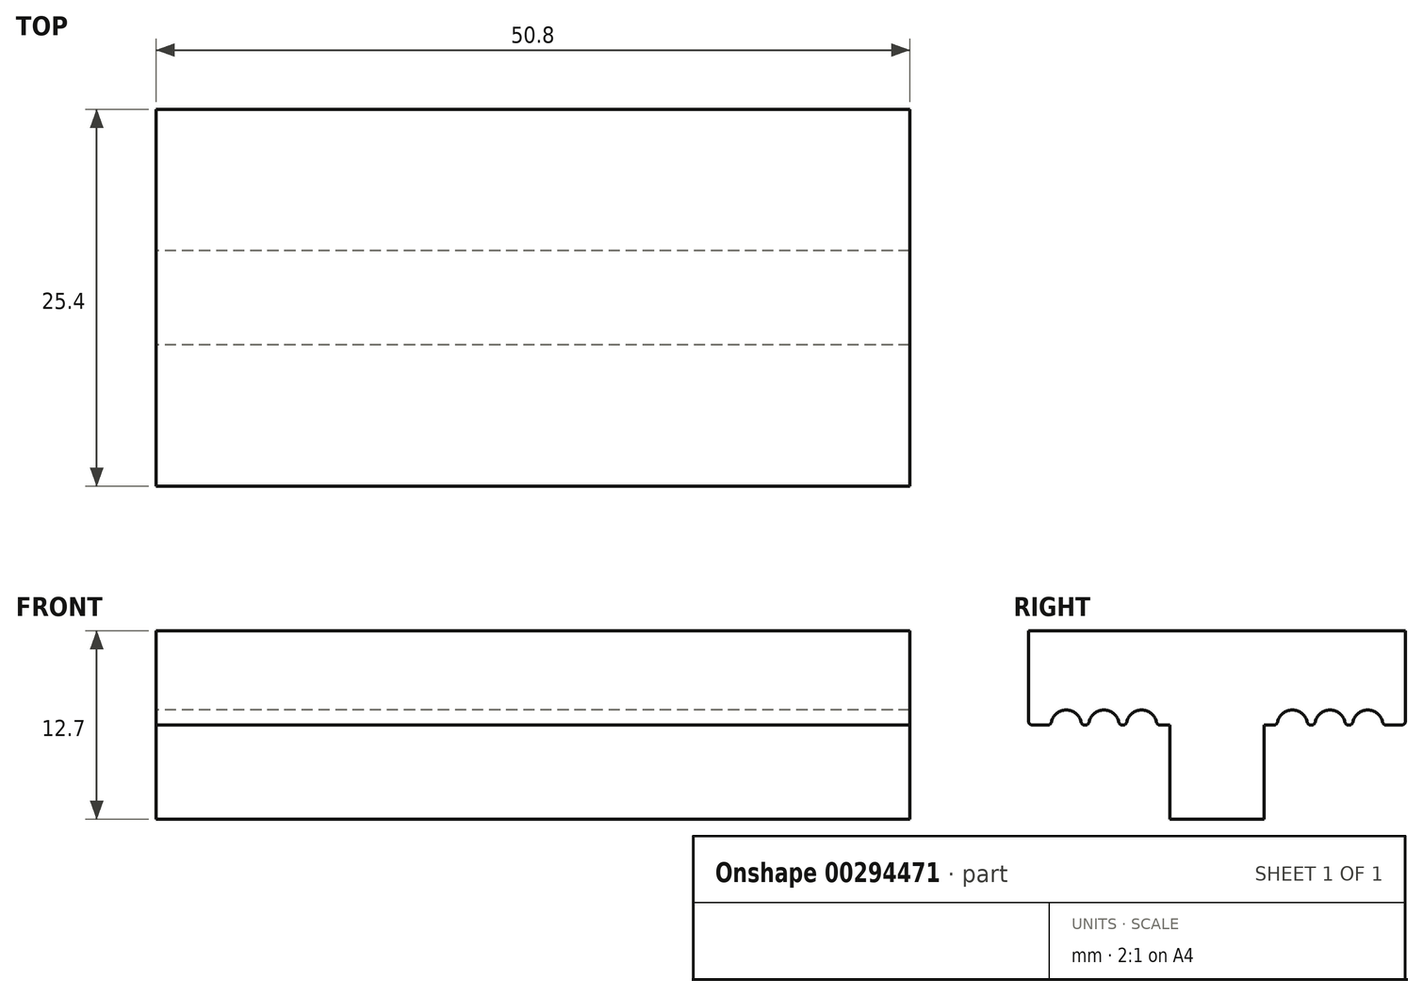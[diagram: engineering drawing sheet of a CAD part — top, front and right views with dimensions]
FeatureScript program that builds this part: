
annotation { "Feature Type Name" : "Feature", "Feature Type Description" : "" }
export const myFeature = defineFeature(function(context is Context, id is Id, definition is map)
    precondition{}
    {
        {
            var Q0;
            Q0=qCreatedBy(makeId("Right.planeOp"),FACE);
            var sketch = newSketch(context, id + "F0", { "sketchPlane" : qUnion([Q0])});
            skLineSegment(sketch, "E0.bottom", {"start": v(0, 0) * mm, "end": v(9.53, 0) * mm});
            skLineSegment(sketch, "E0.top", {"start": v(0, 6.35) * mm, "end": v(25.4, 6.35) * mm});
            skLineSegment(sketch, "E0.left", {"start": v(0, 0) * mm, "end": v(0, 6.35) * mm});
            skLineSegment(sketch, "E0.right", {"start": v(25.4, 0) * mm, "end": v(25.4, 6.35) * mm});
            skLineSegment(sketch, "E1.top", {"start": v(9.53, -6.35) * mm, "end": v(15.88, -6.35) * mm});
            skLineSegment(sketch, "E1.left", {"start": v(9.53, 0) * mm, "end": v(9.53, -6.35) * mm});
            skLineSegment(sketch, "E1.right", {"start": v(15.88, 0) * mm, "end": v(15.88, -6.35) * mm});
            skLineSegment(sketch, "E2", {"start": v(12.7, 6.35) * mm, "end": v(12.7, -6.35) * mm, "construction": true});
            skLineSegment(sketch, "E3.trimOffspring", {"start": v(15.88, 0) * mm, "end": v(25.4, 0) * mm});
            skArc(sketch, "E4", {"start": v(23.88, 0) * mm, "mid": v(22.86, 1.02) * mm, "end": v(21.84, 0) * mm});
            skArc(sketch, "E5", {"start": v(21.34, 0) * mm, "mid": v(20.32, 1.02) * mm, "end": v(19.3, 0) * mm});
            skArc(sketch, "E6", {"start": v(18.8, 0) * mm, "mid": v(17.78, 1.02) * mm, "end": v(16.76, 0) * mm});
            skArc(sketch, "E7.MirrorCS", {"start": v(1.52, 0) * mm, "mid": v(2.54, 1.02) * mm, "end": v(3.56, 0) * mm});
            skArc(sketch, "E8.MirrorCS", {"start": v(6.6, 0) * mm, "mid": v(7.62, 1.02) * mm, "end": v(8.64, 0) * mm});
            skArc(sketch, "E9.MirrorCS", {"start": v(4.06, 0) * mm, "mid": v(5.08, 1.02) * mm, "end": v(6.1, 0) * mm});
            skSolve(sketch);
        }
        {
            var Q0;
            Q0=makeQuery(id+"F0.imprint","IMPRINT",FACE,{"disambiguationData":[TD([[makeQuery(id+"F0.imprint","IMPRINT",EDGE,{"derivedFrom":sQuery(id+"F0.wireOp",EDGE,"E0.top")}),-1.0]])]});
            extrude(context, id + "F1", {"entities" : qUnion([Q0]), "depth" : 50.8 * mm});
        }
        {
            var Q0;
            {var subQ0=sQuery(id+"F0.wireOp",EDGE,"E4");var subQ1=sQuery(id+"F0.wireOp",EDGE,"E3.trimOffspring");Q0=makeQuery(id+"F1.opExtrude","SWEPT_EDGE",EDGE,{"disambiguationData":[OSD([subQ1,subQ0]),TDD([makeQuery(id+"F0.imprint","INTERSECT",VERTEX,{"disambiguationData":[OD(0.0)],"derivedFrom":[subQ1,subQ0]})])]});}
            var Q1;
            Q1=makeQuery(id+"F1.opExtrude","SWEPT_EDGE",EDGE,{"disambiguationData":[OSD([sQuery(id+"F0.wireOp",EDGE,"E0.right"),sQuery(id+"F0.wireOp",EDGE,"E3.trimOffspring")])]});
            var Q2;
            {var subQ0=sQuery(id+"F0.wireOp",EDGE,"E4");var subQ1=sQuery(id+"F0.wireOp",EDGE,"E3.trimOffspring");Q2=makeQuery(id+"F1.opExtrude","SWEPT_EDGE",EDGE,{"disambiguationData":[OSD([subQ1,subQ0]),TDD([makeQuery(id+"F0.imprint","INTERSECT",VERTEX,{"disambiguationData":[OD(1.0)],"derivedFrom":[subQ1,subQ0]})])]});}
            var Q3;
            {var subQ0=sQuery(id+"F0.wireOp",EDGE,"E5");var subQ1=sQuery(id+"F0.wireOp",EDGE,"E3.trimOffspring");Q3=makeQuery(id+"F1.opExtrude","SWEPT_EDGE",EDGE,{"disambiguationData":[OSD([subQ1,subQ0]),TDD([makeQuery(id+"F0.imprint","INTERSECT",VERTEX,{"disambiguationData":[OD(0.0)],"derivedFrom":[subQ1,subQ0]})])]});}
            var Q4;
            {var subQ0=sQuery(id+"F0.wireOp",EDGE,"E6");var subQ1=sQuery(id+"F0.wireOp",EDGE,"E3.trimOffspring");Q4=makeQuery(id+"F1.opExtrude","SWEPT_EDGE",EDGE,{"disambiguationData":[OSD([subQ1,subQ0]),TDD([makeQuery(id+"F0.imprint","INTERSECT",VERTEX,{"disambiguationData":[OD(0.0)],"derivedFrom":[subQ1,subQ0]})])]});}
            var Q5;
            {var subQ0=sQuery(id+"F0.wireOp",EDGE,"E6");var subQ1=sQuery(id+"F0.wireOp",EDGE,"E3.trimOffspring");Q5=makeQuery(id+"F1.opExtrude","SWEPT_EDGE",EDGE,{"disambiguationData":[OSD([subQ1,subQ0]),TDD([makeQuery(id+"F0.imprint","INTERSECT",VERTEX,{"disambiguationData":[OD(1.0)],"derivedFrom":[subQ1,subQ0]})])]});}
            var Q6;
            {var subQ0=sQuery(id+"F0.wireOp",EDGE,"E8.MirrorCS");var subQ1=sQuery(id+"F0.wireOp",EDGE,"E0.bottom");Q6=makeQuery(id+"F1.opExtrude","SWEPT_EDGE",EDGE,{"disambiguationData":[OSD([subQ1,subQ0]),TDD([makeQuery(id+"F0.imprint","INTERSECT",VERTEX,{"disambiguationData":[OD(1.0)],"derivedFrom":[subQ1,subQ0]})])]});}
            var Q7;
            {var subQ0=sQuery(id+"F0.wireOp",EDGE,"E9.MirrorCS");var subQ1=sQuery(id+"F0.wireOp",EDGE,"E0.bottom");Q7=makeQuery(id+"F1.opExtrude","SWEPT_EDGE",EDGE,{"disambiguationData":[OSD([subQ1,subQ0]),TDD([makeQuery(id+"F0.imprint","INTERSECT",VERTEX,{"disambiguationData":[OD(1.0)],"derivedFrom":[subQ1,subQ0]})])]});}
            var Q8;
            {var subQ0=sQuery(id+"F0.wireOp",EDGE,"E8.MirrorCS");var subQ1=sQuery(id+"F0.wireOp",EDGE,"E0.bottom");Q8=makeQuery(id+"F1.opExtrude","SWEPT_EDGE",EDGE,{"disambiguationData":[OSD([subQ1,subQ0]),TDD([makeQuery(id+"F0.imprint","INTERSECT",VERTEX,{"disambiguationData":[OD(0.0)],"derivedFrom":[subQ1,subQ0]})])]});}
            var Q9;
            {var subQ0=sQuery(id+"F0.wireOp",EDGE,"E7.MirrorCS");var subQ1=sQuery(id+"F0.wireOp",EDGE,"E0.bottom");Q9=makeQuery(id+"F1.opExtrude","SWEPT_EDGE",EDGE,{"disambiguationData":[OSD([subQ1,subQ0]),TDD([makeQuery(id+"F0.imprint","INTERSECT",VERTEX,{"disambiguationData":[OD(1.0)],"derivedFrom":[subQ1,subQ0]})])]});}
            var Q10;
            {var subQ0=sQuery(id+"F0.wireOp",EDGE,"E9.MirrorCS");var subQ1=sQuery(id+"F0.wireOp",EDGE,"E0.bottom");Q10=makeQuery(id+"F1.opExtrude","SWEPT_EDGE",EDGE,{"disambiguationData":[OSD([subQ1,subQ0]),TDD([makeQuery(id+"F0.imprint","INTERSECT",VERTEX,{"disambiguationData":[OD(0.0)],"derivedFrom":[subQ1,subQ0]})])]});}
            var Q11;
            {var subQ0=sQuery(id+"F0.wireOp",EDGE,"E7.MirrorCS");var subQ1=sQuery(id+"F0.wireOp",EDGE,"E0.bottom");Q11=makeQuery(id+"F1.opExtrude","SWEPT_EDGE",EDGE,{"disambiguationData":[OSD([subQ1,subQ0]),TDD([makeQuery(id+"F0.imprint","INTERSECT",VERTEX,{"disambiguationData":[OD(0.0)],"derivedFrom":[subQ1,subQ0]})])]});}
            var Q12;
            Q12=makeQuery(id+"F1.opExtrude","SWEPT_EDGE",EDGE,{"disambiguationData":[OSD([sQuery(id+"F0.wireOp",EDGE,"E0.bottom"),sQuery(id+"F0.wireOp",EDGE,"E0.left")])]});
            var Q13;
            {var subQ0=sQuery(id+"F0.wireOp",EDGE,"E5");var subQ1=sQuery(id+"F0.wireOp",EDGE,"E3.trimOffspring");Q13=makeQuery(id+"F1.opExtrude","SWEPT_EDGE",EDGE,{"disambiguationData":[OSD([subQ1,subQ0]),TDD([makeQuery(id+"F0.imprint","INTERSECT",VERTEX,{"disambiguationData":[OD(1.0)],"derivedFrom":[subQ1,subQ0]})])]});}
            fillet(context, id + "F2", {"entities" : qUnion([Q0, Q1, Q2, Q3, Q4, Q5, Q6, Q7, Q8, Q9, Q10, Q11, Q12, Q13]), "radius" : 0.25 * mm, "tangentPropagation" : true, "allowEdgeOverflow" : false});
        }
    });
